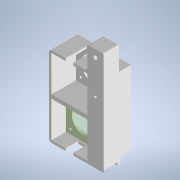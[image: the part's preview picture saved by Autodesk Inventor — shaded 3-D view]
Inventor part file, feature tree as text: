
AUTODESK INVENTOR PART (.ipt)
format: ipt  version: 2022 (Build 260153000, 153)  size: 445,952 bytes
history: native  units: mm
features: sketch x17, reference x17, extrude x16, projected_geometry x15, plane x4, other x3, hole x2, fillet x1, chamfer x1
ambient origin geometry x8: Origin, YZ Plane, XZ Plane, XY Plane, X Axis, Y Axis, Z Axis, Center Point
bodies: Solid1 (feature_tree)
feature tree (76):
  extrude  "Extrusion1"  Depth=180.0mm
  fillet  "Fillet1"  Radius=18.0mm
  extrude  "Extrusion2"  Depth=20.0mm
  extrude  "Extrusion4"  Depth=9.0mm TaperAngle=0.0deg
  sketch  "Sketch5"  dims[d6=12.0mm d8=9.0mm d9=0.0mm]
  plane  "Work Plane1"
  plane  "Work Plane3"
  extrude  "Extrusion5"  Depth=3.0mm
  extrude  "Extrusion6"  Depth=10.0mm
  plane  "Work Plane2"
  extrude  "Extrusion7"  Depth=79.0mm
  extrude  "Extrusion8"  TaperAngle=0.0deg  [1 undecoded]
  extrude  "Extrusion9"  Depth=3.0mm TaperAngle=0.0deg
  extrude  "Extrusion10"  Depth=3.0mm TaperAngle=0.0deg
  extrude  "Extrusion11"  Depth=3.0mm TaperAngle=0.0deg
  sketch  "Sketch12"  dims[d31=3.0mm d32=0.0mm d33=3.0mm d34=0.0mm]
  plane  "Work Plane4"
  extrude  "Extrusion12"  Depth=0.25mm
  chamfer  "Chamfer1"  Distance=3.0mm
  hole  "Hole1"  [1 undecoded]
  extrude  "Extrusion13"  Depth=10.0mm TaperAngle=0.0deg
  sketch  "Sketch15"  dims[d44=2.5mm d45=6.0mm d46=5.0mm d47=20.0mm d48=90.0deg d49=8.0mm d50=20.594885mm d51=10.0mm d52=0.0mm]
  extrude  "Extrusion15"  Depth=5.0mm
  extrude  "Extrusion16"  Depth=15.0mm TaperAngle=0.0deg
  extrude  "Extrusion17"  TaperAngle=0.0deg  [1 undecoded]
  extrude  "Extrusion18"  Depth=7.0mm
  hole  "Bohrung2"  [1 undecoded]
  sketch  "Sketch2"  dims[d0=19.7mm d1=180.0mm d2=18.0mm d3=0.0mm]
  projected_geometry  "Projected Loop1"
  sketch  "Sketch4"  dims[d4=2.0mm d5=20.0mm]
  projected_geometry  "Projected Loop3"
  projected_geometry  "Projected Loop4"
  reference  "Reference1"
  reference  "Reference2"
  reference  "Reference3"
  reference  "Reference4"
  reference  "Reference5"
  reference  "Reference6"
  sketch  "Sketch6"  dims[d14=3.0mm d15=3.0mm]
  projected_geometry  "Projected Loop5"
  reference  "Reference7"
  reference  "Reference8"
  reference  "Reference9"
  reference  "Reference10"
  reference  "Reference11"
  sketch  "Sketch7"  dims[d16=10.0mm d17=10.0mm]
  projected_geometry  "Projected Loop6"
  reference  "Reference12"
  reference  "Reference13"
  reference  "Reference14"
  reference  "Reference15"
  reference  "Reference16"
  sketch  "Sketch8"  dims[d18=49.0mm d19=79.0mm]
  projected_geometry  "Projected Loop7"
  sketch  "Sketch9"  dims[d20=110.0mm d21=0.0mm d22=0.0mm]
  projected_geometry  "Projected Loop8"
  sketch  "Sketch10"  dims[d23=10.0mm d24=0.0mm d25=3.0mm d26=0.0mm]
  projected_geometry  "Projected Loop9"
  sketch  "Sketch11"  dims[d27=3.0mm d28=0.0mm d29=3.0mm d30=0.0mm]
  projected_geometry  "Projected Loop10"
  projected_geometry  "Projected Loop11"
  sketch  "Sketch13"  dims[d35=0.25mm d36=0.25mm d37=3.0mm d38=0.0mm]
  sketch  "Sketch14"  dims[d39=10.0mm d40=0.0mm d41=2.0mm d42=2.0mm d43=45.0deg]
  projected_geometry  "Projected Loop12"
  reference  "Reference17"
  sketch  "Skizze16"  dims[d53=142.0mm d54=5.0mm]
  projected_geometry  "Projizierte Kontur13"
  sketch  "Skizze17"  dims[d55=8.9mm d58=15.0mm d59=0.0mm]
  projected_geometry  "Projizierte Kontur14"
  sketch  "Skizze18"  dims[d60=25.0mm d61=0.0mm d62=0.0mm d63=0.0mm]
  projected_geometry  "Projizierte Kontur15"
  sketch  "Skizze19"  dims[d66=7.0mm d67=7.0mm d68=100.0mm d69=0.0mm d70=9.5mm d71=50.0mm d72=60.0mm d73=4.5mm d74=6.0mm d75=9.0mm d76=15.0mm d77=90.0deg d78=8.0mm d79=20.594885mm]
  projected_geometry  "Projizierte Kontur17"
  other  "Assembly_XYTable_Aliepexress.iam"
  other  "00_NEMA17:2"
  other  "00_NEMA17:1"
note: 4 required parameter values undecoded (feature->parameter linkage not recoverable at this tier; creation-order binding heuristic only, values carry confidence <= 0.55)
